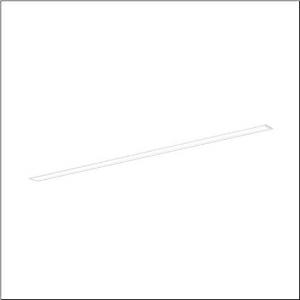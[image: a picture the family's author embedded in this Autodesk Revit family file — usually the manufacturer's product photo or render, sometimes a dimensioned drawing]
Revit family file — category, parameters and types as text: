
# Revit family: silica_21_51mx13db35wb
name_source: partatom
category: Lighting Fixtures
units: mm (PartAtom-declared; Revit-internal decimal feet)

## family parameters
Cut with Voids When Loaded = No
Host = Face
Light Source = No
Part Type = Normal
Room Calculation Point = No
Round Connector Dimension = Use Diameter
Shared = No

## types (1)
- --- (1 x LED, 4100 lm, 30.1 W, 3000K)
    Apparent Load = 30 VA
    CIE Flux Codes = 78 96 99 100 100
    Color Rendering = 80
    Color Temperature = 3000K
    Default Elevation = 1800 mm
    Description = Silica 21, office luminaire, primary optical cover: prismatic diffuser, of PMMA, CAT 2 (L<= 3000cd/m²), light emission: direct distribution, primary light characteristic: symmetric, installation type: recessed, LED, rated luminous flux: 4.100lm, luminous efficacy: 136lm/W, light colour: 830, colour temperature: 3000K, control gear: DALI 2, with terminal, 3+2-pole, max. 2.5mm², mains connection: 220..240V, AC, 50/60Hz, rated input power: 30.1W, luminaire housing, of aluminium, traffic white (RAL 9016), length: 1.528mm, width: 79mm, height: 53mm, protection rating (complete): IP20, insulation class (complete): insulation class I (protective earthing), certification: CE, ENEC, VDE, permissible operating ambient temperature: 0..+35°C, standard: EN 50419, packaging unit: 1 piece
    Height = 0 mm  [stored 0 ft]
    Lamp = 1 x LED
    Lamp Light Flux = 4100 lm
    Lamp Power = 30.1 W
    Lamp count = 1
    Length = 1527 mm
    Luminous efficacy = 136 lm/W
    Manufacturer = Siteco
    ModVariant = No
    Model = 51MX13DB35WB
    Mounting Place = Ceiling
    Mounting Type = Recessed
    Number of Poles = 1
    OnlyDefault = Yes
    Power Factor = 1
    Product Name = Silica 21
    Product group = office luminaire | ceiling recessed
    ProductGroupID = 400
    Protection Class = Protection class I
    Protection Degree = IP 20
    RLX_Detail_Level = 1
    RLX_Emergency_Light_Flux = 0 lm
    RLX_Emergency_Type = 0
    RLX_Emergency_Type_DB = No
    RlxData = <blob elided: 14221 chars, md5=60843d71>
    Socket = socket
    Standby Power = 0 W
    System Light Flux = 4100 lm
    System Power = 30 W
    Type Comments = factory setting: luminous flux: 100 % | dim-lin: 254 | 345 mA
    Type Image = l_1251692.jpg
    URL = http://relux.com
    VarID = @adj_119211
    Voltage = 0 V
    Weight = 0.00 kg
    Width = 79 mm

note: [stored X ft] marks values corroborated as IEEE doubles in the binary element streams (Revit-internal decimal feet)

## geometry (parser evidence)
native form markers: Sweep x11
no freeform markers — native parametric forms only
